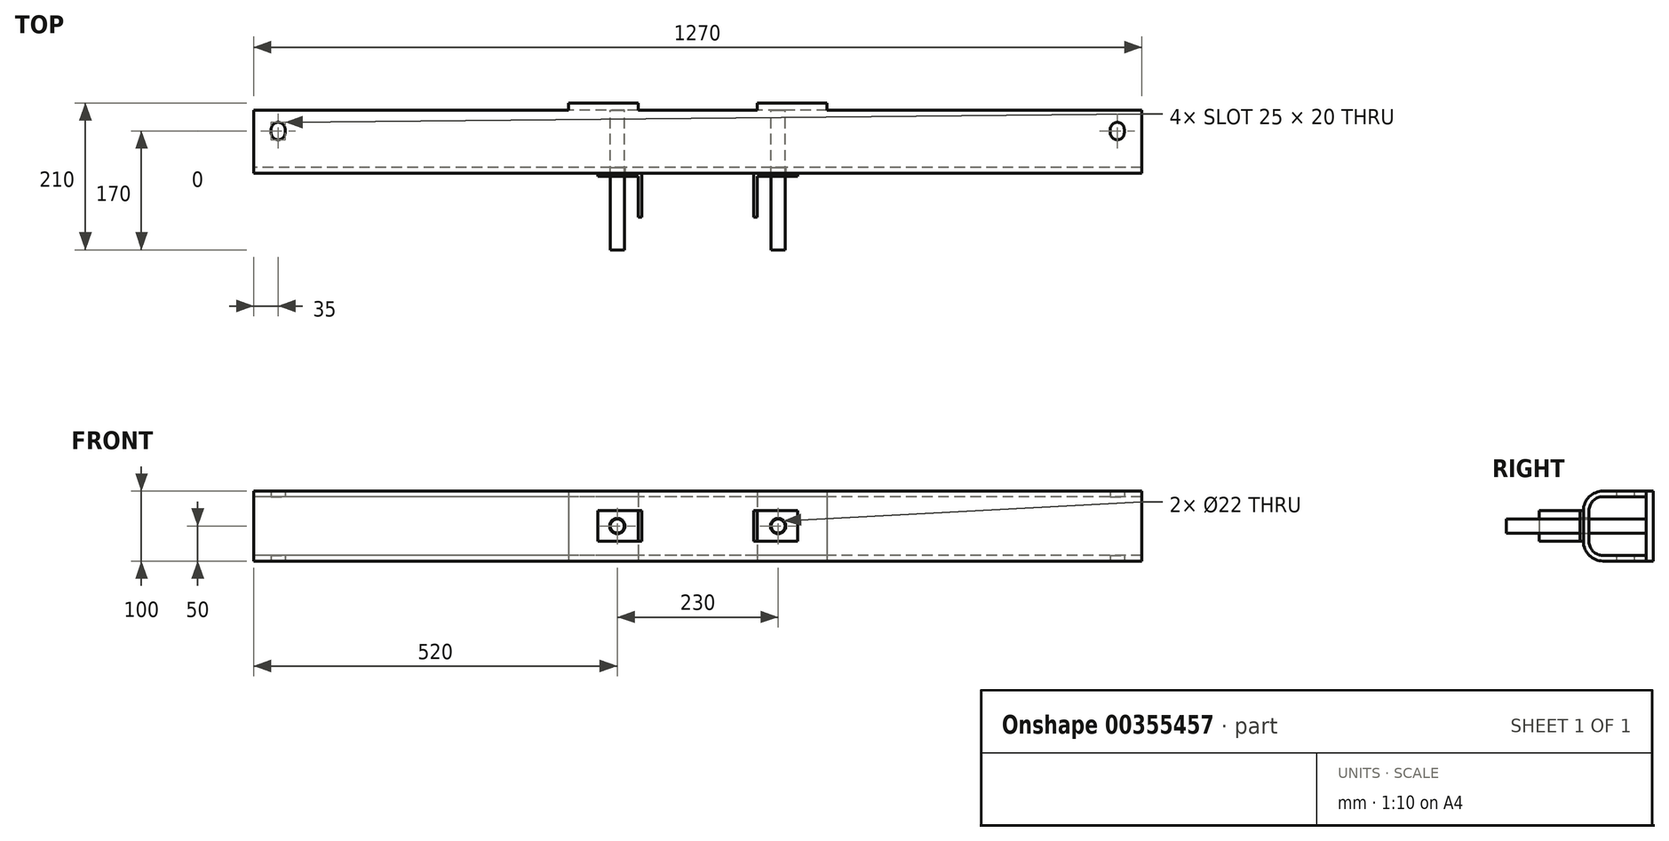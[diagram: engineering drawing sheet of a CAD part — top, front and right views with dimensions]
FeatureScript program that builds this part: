
annotation { "Feature Type Name" : "Feature", "Feature Type Description" : "" }
export const myFeature = defineFeature(function(context is Context, id is Id, definition is map)
    precondition{}
    {
        {
            var Q0;
            Q0=qCreatedBy(makeId("Right.planeOp"),FACE);
            var sketch = newSketch(context, id + "F0", { "sketchPlane" : qUnion([Q0])});
            skLineSegment(sketch, "E0", {"start": v(90, 50) * mm, "end": v(28, 50) * mm});
            skLineSegment(sketch, "E1", {"start": v(0, 22) * mm, "end": v(0, -22) * mm});
            skLineSegment(sketch, "E2", {"start": v(28, -50) * mm, "end": v(90, -50) * mm});
            skLineSegment(sketch, "E3", {"start": v(90, -50) * mm, "end": v(90, -42) * mm});
            skLineSegment(sketch, "E4", {"start": v(90, -42) * mm, "end": v(28, -42) * mm});
            skLineSegment(sketch, "E5", {"start": v(8, -22) * mm, "end": v(8, 22) * mm});
            skLineSegment(sketch, "E6", {"start": v(28, 42) * mm, "end": v(90, 42) * mm});
            skLineSegment(sketch, "E7", {"start": v(90, 42) * mm, "end": v(90, 50) * mm});
            skPoint(sketch, "E8.visualSharp", {"position": v(8, 42) * mm});
            skArc(sketch, "E8.filletArc", {"start": v(28, 42) * mm, "mid": v(13.86, 36.14) * mm, "end": v(8, 22) * mm});
            skPoint(sketch, "E9.visualSharp", {"position": v(8, -42) * mm});
            skArc(sketch, "E9.filletArc", {"start": v(8, -22) * mm, "mid": v(13.86, -36.14) * mm, "end": v(28, -42) * mm});
            skPoint(sketch, "E10.visualSharp", {"position": v(0, 50) * mm});
            skArc(sketch, "E10.filletArc", {"start": v(28, 50) * mm, "mid": v(8.2, 41.8) * mm, "end": v(0, 22) * mm});
            skPoint(sketch, "E11.visualSharp", {"position": v(0, -50) * mm});
            skArc(sketch, "E11.filletArc", {"start": v(0, -22) * mm, "mid": v(8.2, -41.8) * mm, "end": v(28, -50) * mm});
            skSolve(sketch);
        }
        {
            var Q0;
            Q0=qSketchRegion(id+"F0",true);
            extrude(context, id + "F1", {"entities" : qUnion([Q0]), "endBound" : BoundingType.SYMMETRIC, "depth" : 1270 * mm});
        }
        {
            var Q0;
            Q0=qCreatedBy(makeId("Top.planeOp"),FACE);
            var sketch = newSketch(context, id + "F2", { "sketchPlane" : qUnion([Q0])});
            skLineSegment(sketch, "E12", {"start": v(-143, 0) * mm, "end": v(-80, 0) * mm});
            skLineSegment(sketch, "E13", {"start": v(-80, 0) * mm, "end": v(-80, -63) * mm});
            skLineSegment(sketch, "E14.0", {"start": v(-85, -5) * mm, "end": v(-85, -63) * mm});
            skLineSegment(sketch, "E14.1", {"start": v(-143, -5) * mm, "end": v(-85, -5) * mm});
            skLineSegment(sketch, "E15", {"start": v(-143, -5) * mm, "end": v(-143, 0) * mm});
            skLineSegment(sketch, "E16", {"start": v(-85, -63) * mm, "end": v(-80, -63) * mm});
            skLineSegment(sketch, "E17.MirrorCS", {"start": v(85, -63) * mm, "end": v(80, -63) * mm});
            skLineSegment(sketch, "E18.MirrorCS", {"start": v(143, -5) * mm, "end": v(143, 0) * mm});
            skLineSegment(sketch, "E19.MirrorCS", {"start": v(143, 0) * mm, "end": v(80, 0) * mm});
            skLineSegment(sketch, "E20.MirrorCS", {"start": v(80, 0) * mm, "end": v(80, -63) * mm});
            skLineSegment(sketch, "E21.MirrorCS", {"start": v(143, -5) * mm, "end": v(85, -5) * mm});
            skLineSegment(sketch, "E22.MirrorCS", {"start": v(85, -5) * mm, "end": v(85, -63) * mm});
            skSolve(sketch);
        }
        {
            var Q0;
            Q0=qSketchRegion(id+"F2",true);
            extrude(context, id + "F3", {"entities" : qUnion([Q0]), "operationType" : NewBodyOperationType.ADD, "endBound" : BoundingType.SYMMETRIC, "depth" : 44 * mm});
        }
        {
            var Q0;
            Q0=makeQuery(id+"F1.opExtrude","SWEPT_FACE",FACE,{"disambiguationData":[OSD([sQuery(id+"F0.wireOp",EDGE,"E7")])]});
            var sketch = newSketch(context, id + "F4", { "sketchPlane" : qUnion([Q0])});
            skLineSegment(sketch, "E23.bottom", {"start": v(-185, 50) * mm, "end": v(-85, 50) * mm});
            skLineSegment(sketch, "E23.top", {"start": v(-185, -50) * mm, "end": v(-85, -50) * mm});
            skLineSegment(sketch, "E23.left", {"start": v(-185, 50) * mm, "end": v(-185, -50) * mm});
            skLineSegment(sketch, "E23.right", {"start": v(-85, 50) * mm, "end": v(-85, -50) * mm});
            skLineSegment(sketch, "E24.MirrorCS", {"start": v(85, 50) * mm, "end": v(85, -50) * mm});
            skLineSegment(sketch, "E25.MirrorCS", {"start": v(185, 50) * mm, "end": v(185, -50) * mm});
            skLineSegment(sketch, "E26.MirrorCS", {"start": v(185, 50) * mm, "end": v(85, 50) * mm});
            skLineSegment(sketch, "E27.MirrorCS", {"start": v(185, -50) * mm, "end": v(85, -50) * mm});
            skSolve(sketch);
        }
        {
            var Q0;
            Q0=qSketchRegion(id+"F4",true);
            extrude(context, id + "F5", {"entities" : qUnion([Q0]), "operationType" : NewBodyOperationType.ADD, "depth" : 10 * mm});
        }
        {
            var Q0;
            Q0=qCreatedBy(makeId("Front.planeOp"),FACE);
            var sketch = newSketch(context, id + "F6", { "sketchPlane" : qUnion([Q0])});
            skCircle(sketch, "E28", {"center": v(-115, 0) * mm, "radius": 11 * mm});
            skCircle(sketch, "E29.MirrorC", {"center": v(115, 0) * mm, "radius": 11 * mm});
            skSolve(sketch);
        }
        {
            var Q0;
            Q0=qSketchRegion(id+"F6",true);
            extrude(context, id + "F7", {"entities" : qUnion([Q0]), "operationType" : NewBodyOperationType.REMOVE, "endBound" : BoundingType.UP_TO_NEXT, "oppositeDirection" : true, "depth" : 25 * mm, "hasSecondDirection" : true, "secondDirectionBound" : SecondDirectionBoundingType.THROUGH_ALL, "secondDirectionOppositeDirection" : false, "secondDirectionDepth" : 25 * mm});
        }
        {
            var Q0;
            Q0=qCreatedBy(makeId("Top.planeOp"),FACE);
            var sketch = newSketch(context, id + "F8", { "sketchPlane" : qUnion([Q0])});
            skArc(sketch, "E30", {"start": v(-590, 62.5) * mm, "mid": v(-600, 72.5) * mm, "end": v(-610, 62.5) * mm});
            skLineSegment(sketch, "E31", {"start": v(-610, 62.5) * mm, "end": v(-610, 57.5) * mm});
            skLineSegment(sketch, "E32", {"start": v(-590, 62.5) * mm, "end": v(-590, 57.5) * mm});
            skArc(sketch, "E33", {"start": v(-610, 57.5) * mm, "mid": v(-600, 47.5) * mm, "end": v(-590, 57.5) * mm});
            skLineSegment(sketch, "E34.MirrorCS", {"start": v(590, 62.5) * mm, "end": v(590, 57.5) * mm});
            skLineSegment(sketch, "E35.MirrorCS", {"start": v(610, 62.5) * mm, "end": v(610, 57.5) * mm});
            skArc(sketch, "E36.MirrorCS", {"start": v(610, 57.5) * mm, "mid": v(600, 47.5) * mm, "end": v(590, 57.5) * mm});
            skArc(sketch, "E37.MirrorCS", {"start": v(590, 62.5) * mm, "mid": v(600, 72.5) * mm, "end": v(610, 62.5) * mm});
            skSolve(sketch);
        }
        {
            var Q0;
            Q0=qSketchRegion(id+"F8",true);
            extrude(context, id + "F9", {"entities" : qUnion([Q0]), "operationType" : NewBodyOperationType.REMOVE, "endBound" : BoundingType.THROUGH_ALL, "depth" : 25 * mm, "hasSecondDirection" : true, "secondDirectionBound" : SecondDirectionBoundingType.THROUGH_ALL, "secondDirectionOppositeDirection" : true, "secondDirectionDepth" : 25 * mm});
        }
        {
            var Q0;
            Q0=makeQuery(id+"F5.opExtrude","CAP_FACE",FACE,{"disambiguationData":[OSD([sQuery(id+"F4.wireOp",EDGE,"E24.MirrorCS"),sQuery(id+"F4.wireOp",EDGE,"E25.MirrorCS"),sQuery(id+"F4.wireOp",EDGE,"E26.MirrorCS"),sQuery(id+"F4.wireOp",EDGE,"E27.MirrorCS")])],"isStart":true});
            var sketch = newSketch(context, id + "F10", { "sketchPlane" : qUnion([Q0])});
            skCircle(sketch, "E38", {"center": v(-115, 0) * mm, "radius": 10 * mm});
            skCircle(sketch, "E39.MirrorC", {"center": v(115, 0) * mm, "radius": 10 * mm});
            skSolve(sketch);
        }
        {
            var Q0;
            Q0=qSketchRegion(id+"F10",true);
            extrude(context, id + "F11", {"entities" : qUnion([Q0]), "operationType" : NewBodyOperationType.ADD, "depth" : 200 * mm});
        }
    });
